SOLIDWORKS PART (.sldprt)
format: sldprt  version: not decoded by parser v0  size: 360,960 bytes
history: native  units: mm
features: sketch x3, extrude x2, material x1, fillet x1, cut_extrude x1 (+13 scaffold rows collapsed)
feature tree (21):
  scaffold x13  (default folders/planes/origin — collapsed)
  material  "Material <not specified>"
  sketch  "Sketch1"  dims[D1=5.0mm D2=5.0mm D3=5.0mm D4=5.0mm D5=5.0mm]
  extrude  "Boss-Extrude1"  Depth=1mm
  sketch  "Sketch2"  dims[c1.D1=2.0mm c1.D7=2.0mm c1.D2=4.0mm c1.D3=4.0mm c2.D7=17.2mm c2.D8=1.0mm c2.D4=7.0 c2.D5=7.0 c2.D6=11.0]
  extrude  "Boss-Extrude2"  Depth=1mm
  fillet  "Fillet1"  Radius=3mm
  sketch  "Sketch3"  dims[D1=3.1mm D2=3.1mm]
  cut_extrude  "Cut-Extrude1"  [1 undecoded]
decode coverage: 6 of 7 modeling features carry decoded parameters
note: 1 parameter value undecoded
note: suppression state not decoded; provenance and decode notes live in map.json
